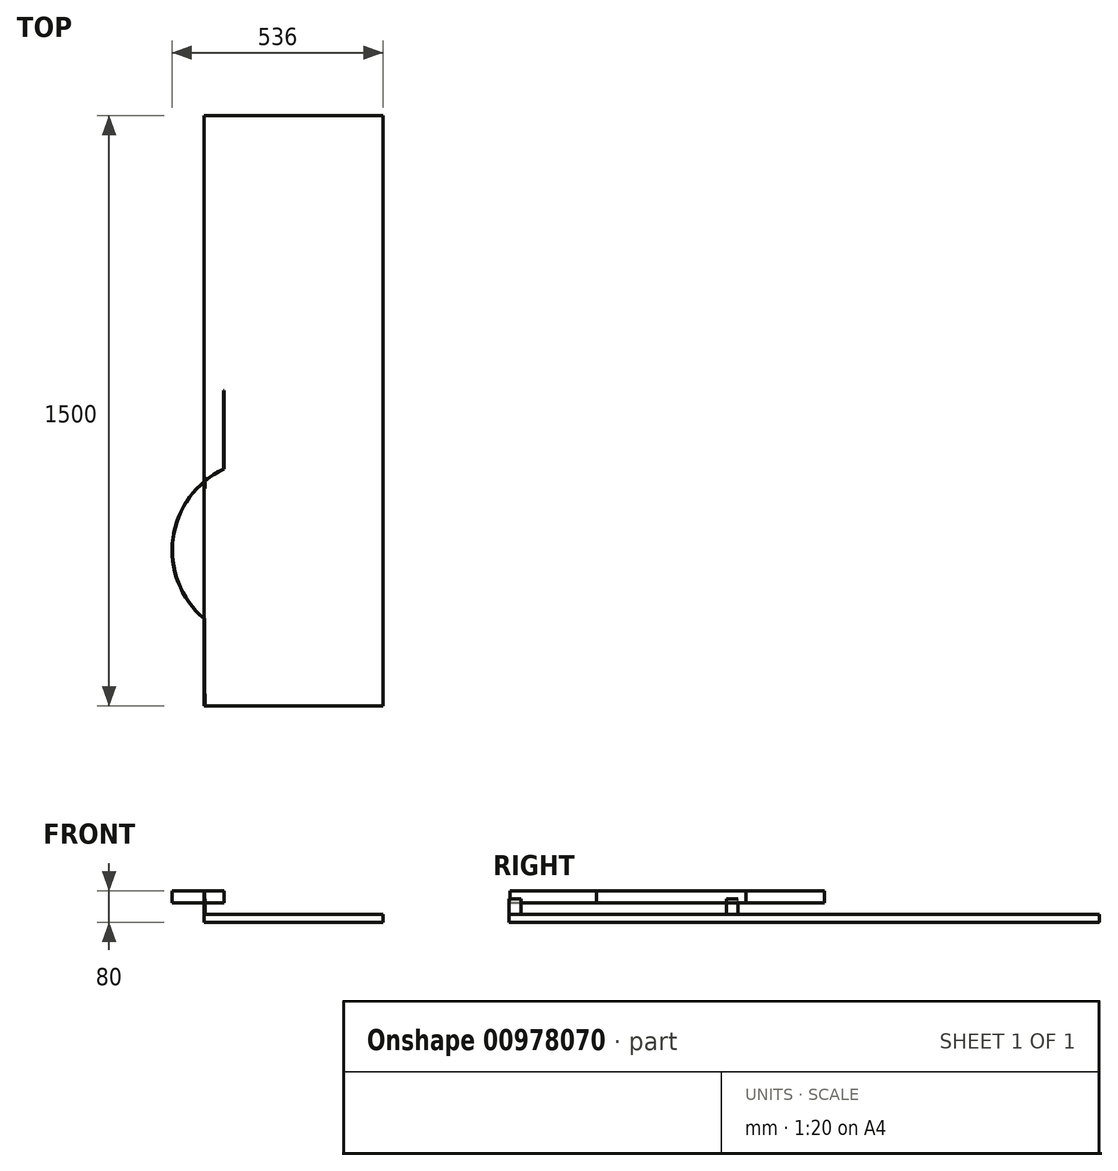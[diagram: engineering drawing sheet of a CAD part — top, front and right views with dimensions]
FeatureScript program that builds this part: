
annotation { "Feature Type Name" : "Feature", "Feature Type Description" : "" }
export const myFeature = defineFeature(function(context is Context, id is Id, definition is map)
    precondition{}
    {
        {
            var Q0;
            Q0=qCreatedBy(makeId("Top.planeOp"),FACE);
            var sketch = newSketch(context, id + "F0", { "sketchPlane" : qUnion([Q0])});
            skLineSegment(sketch, "E0.bottom", {"start": v(0, 0) * mm, "end": v(455, 0) * mm});
            skLineSegment(sketch, "E0.top", {"start": v(0, 1500) * mm, "end": v(455, 1500) * mm});
            skLineSegment(sketch, "E0.left", {"start": v(0, 0) * mm, "end": v(0, 1500) * mm});
            skLineSegment(sketch, "E0.right", {"start": v(455, 0) * mm, "end": v(455, 1500) * mm});
            skSolve(sketch);
        }
        {
            var Q0;
            Q0=qSketchRegion(id+"F0",true);
            extrude(context, id + "F1", {"entities" : qUnion([Q0]), "depth" : 20 * mm, "offsetDistance" : 25 * mm});
        }
        {
            var Q0;
            Q0=qCreatedBy(makeId("Top.planeOp"),FACE);
            cPlane(context, id + "F5", {"entities" : qUnion([Q0]), "cplaneType" : CPlaneType.OFFSET, "offset" : 50 * mm, "width" : 150 * mm, "height" : 150 * mm});
        }
        {
            var Q0;
            Q0=qCreatedBy(id+"F5.planeOp",FACE);
            var sketch = newSketch(context, id + "F6", { "sketchPlane" : qUnion([Q0])});
            skLineSegment(sketch, "E1", {"start": v(50, 601.81) * mm, "end": v(50, 801.81) * mm});
            skLineSegment(sketch, "E2", {"start": v(50, 801.81) * mm, "end": v(51, 801.81) * mm});
            skLineSegment(sketch, "E3", {"start": v(51, 801.81) * mm, "end": v(51, 601.81) * mm});
            skLineSegment(sketch, "E4", {"start": v(0, 1.81) * mm, "end": v(0, 221.81) * mm});
            skLineSegment(sketch, "E5", {"start": v(1, 221.81) * mm, "end": v(1, 1.81) * mm});
            skLineSegment(sketch, "E6", {"start": v(1, 1.81) * mm, "end": v(0, 1.81) * mm});
            skArc(sketch, "E7", {"start": v(50, 601.81) * mm, "mid": v(-79.06, 425.5) * mm, "end": v(0, 221.81) * mm});
            skArc(sketch, "E8", {"start": v(51, 601.81) * mm, "mid": v(-78.06, 425.5) * mm, "end": v(1, 221.81) * mm});
            skSolve(sketch);
        }
        {
            var Q0;
            Q0 = qSketchRegion(id + "F6", true);
            extrude(context, id + "F7", {"entities" : qUnion([Q0]), "depth" : 30 * mm, "offsetDistance" : 25 * mm});
        }
        {
            var Q0;
            Q0=qCreatedBy(makeId("Right.planeOp"),FACE);
            var sketch = newSketch(context, id + "F8", { "sketchPlane" : qUnion([Q0])});
            skLineSegment(sketch, "E9.bottom", {"start": v(0, 20) * mm, "end": v(30, 20) * mm});
            skLineSegment(sketch, "E9.top", {"start": v(0, 60) * mm, "end": v(30, 60) * mm});
            skLineSegment(sketch, "E9.left", {"start": v(0, 20) * mm, "end": v(0, 60) * mm});
            skLineSegment(sketch, "E9.right", {"start": v(30, 20) * mm, "end": v(30, 60) * mm});
            skLineSegment(sketch, "E10.bottom", {"start": v(552.13, 20) * mm, "end": v(582.13, 20) * mm});
            skLineSegment(sketch, "E10.top", {"start": v(552.13, 60) * mm, "end": v(582.13, 60) * mm});
            skLineSegment(sketch, "E10.left", {"start": v(552.13, 20) * mm, "end": v(552.13, 60) * mm});
            skLineSegment(sketch, "E10.right", {"start": v(582.13, 20) * mm, "end": v(582.13, 60) * mm});
            skSolve(sketch);
        }
        {
            var Q0;
            Q0 = qSketchRegion(id + "F8", true);
            extrude(context, id + "F9", {"entities" : qUnion([Q0]), "depth" : 3 * mm, "offsetDistance" : 25 * mm});
        }
    });
